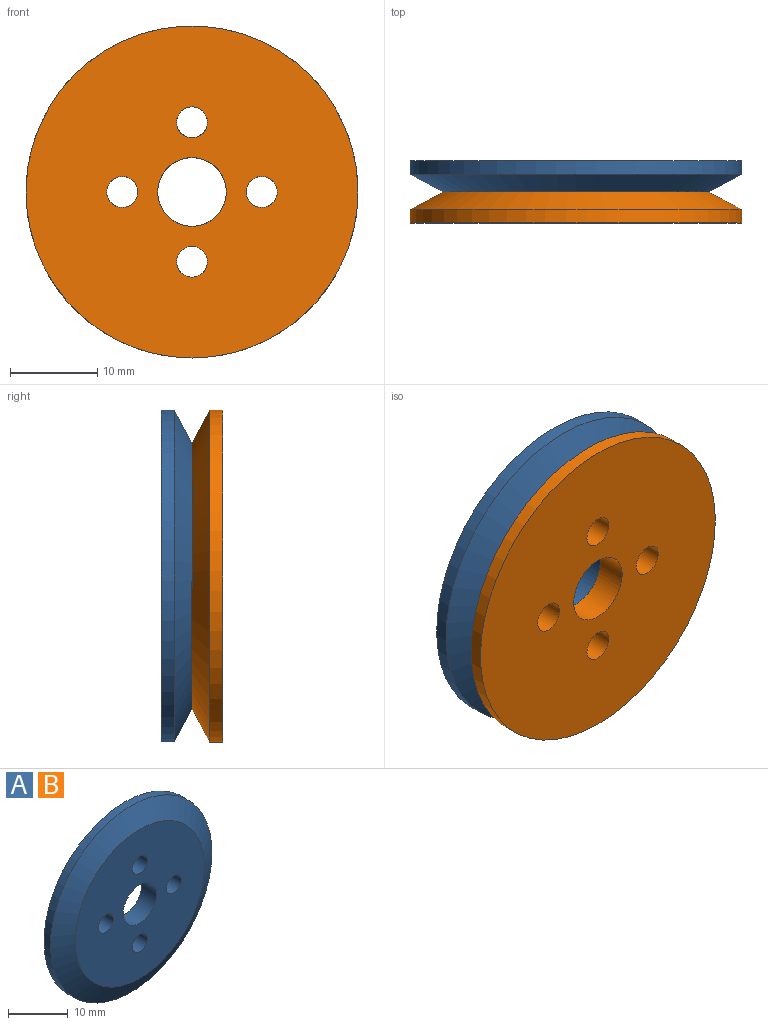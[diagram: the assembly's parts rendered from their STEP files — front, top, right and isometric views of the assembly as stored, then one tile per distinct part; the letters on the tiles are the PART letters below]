
ASSEMBLY  parts=2 mates=1
PART A: 9 faces, bbox 38.1x3.6x38.1 mm
  f0: plane 30.48x30.48mm, normal (0,-1,0), area 641.2mm2, adj f3,f4,f5,f6,f7,f8
  f1: plane 38.1x38.1mm, normal (0,1,0), area 1051.7mm2, adj f2,f4,f5,f6,f7,f8
  f2: cylinder r=19.05mm len=38.1mm, axis (0,1,0), area 182.4mm2, adj f1,f3
  f3: cone r=15.24mm half-angle=61.9deg, axis (0,1,0), area 465.2mm2, adj f0,f2
  f4: cylinder r=1.78mm len=3.56mm, axis (0,-1,0), area 39.7mm2, adj f0,f1
  f5: cylinder r=1.78mm len=3.56mm, axis (0,-1,0), area 39.7mm2, adj f0,f1
  f6: cylinder r=1.78mm len=3.56mm, axis (0,-1,0), area 39.7mm2, adj f0,f1
  f7: cylinder r=1.78mm len=3.56mm, axis (0,-1,0), area 39.7mm2, adj f0,f1
  f8: cylinder r=3.94mm len=7.87mm, axis (0,-1,0), area 88mm2, adj f0,f1
PART B: same geometry as A
PLACE A t=(-34.43,-16.95,1.73)mm
PLACE B rot(axis=(-1,0,0),180deg) t=(-34.43,-16.95,1.73)mm
MATE fastened A.f2 <-> B.f2  axis (0,-1,0) through (-34.43,-16.95,1.73)mm
